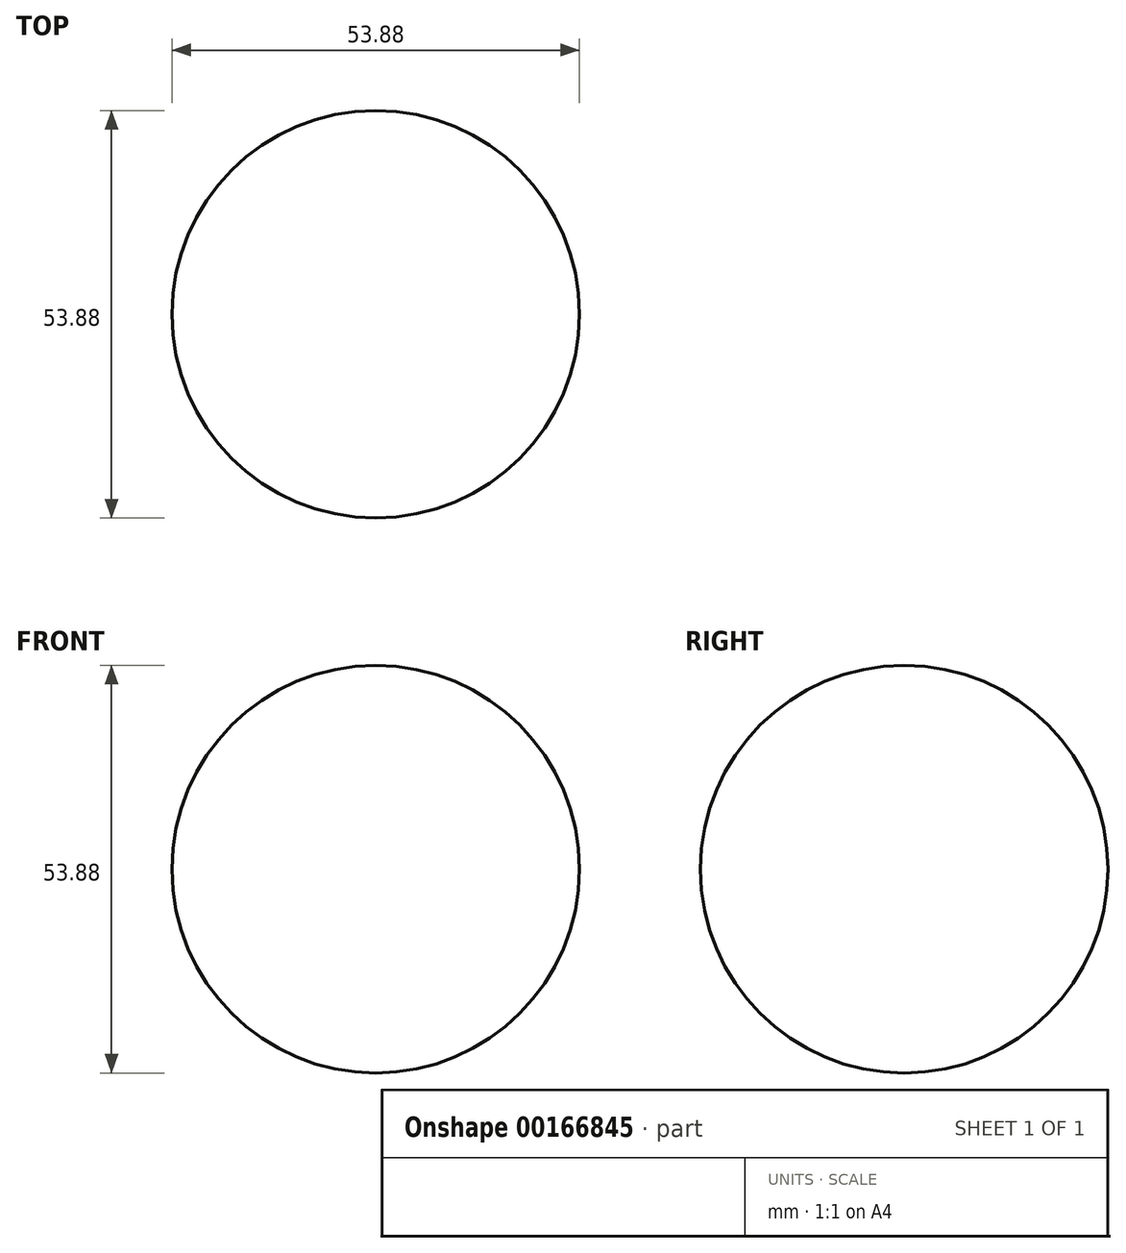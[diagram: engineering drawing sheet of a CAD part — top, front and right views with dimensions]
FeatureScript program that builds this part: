
annotation { "Feature Type Name" : "Feature", "Feature Type Description" : "" }
export const myFeature = defineFeature(function(context is Context, id is Id, definition is map)
    precondition{}
    {
        {
            var Q0;
            Q0=qCreatedBy(makeId("Front.planeOp"),FACE);
            var sketch = newSketch(context, id + "F0", { "sketchPlane" : qUnion([Q0])});
            skArc(sketch, "E0", {"start": v(0, 0) * mm, "mid": v(26.94, 26.94) * mm, "end": v(0, 53.88) * mm});
            skLineSegment(sketch, "E1", {"start": v(0, 53.88) * mm, "end": v(0, 0) * mm});
            skSolve(sketch);
        }
        {
            var Q0;
            Q0=makeQuery(id+"F0.imprint","IMPRINT",FACE,{"disambiguationData":[TD([[makeQuery(id+"F0.imprint","IMPRINT",EDGE,{"derivedFrom":sQuery(id+"F0.wireOp",EDGE,"E0")}),1.0]])]});
            var Q1;
            Q1=sQuery(id+"F0.wireOp",EDGE,"E1");
            revolve(context, id + "F1", {"entities" : qUnion([Q0]), "axis" : qUnion([Q1]), "revolveType" : RevolveType.FULL});
        }
    });
